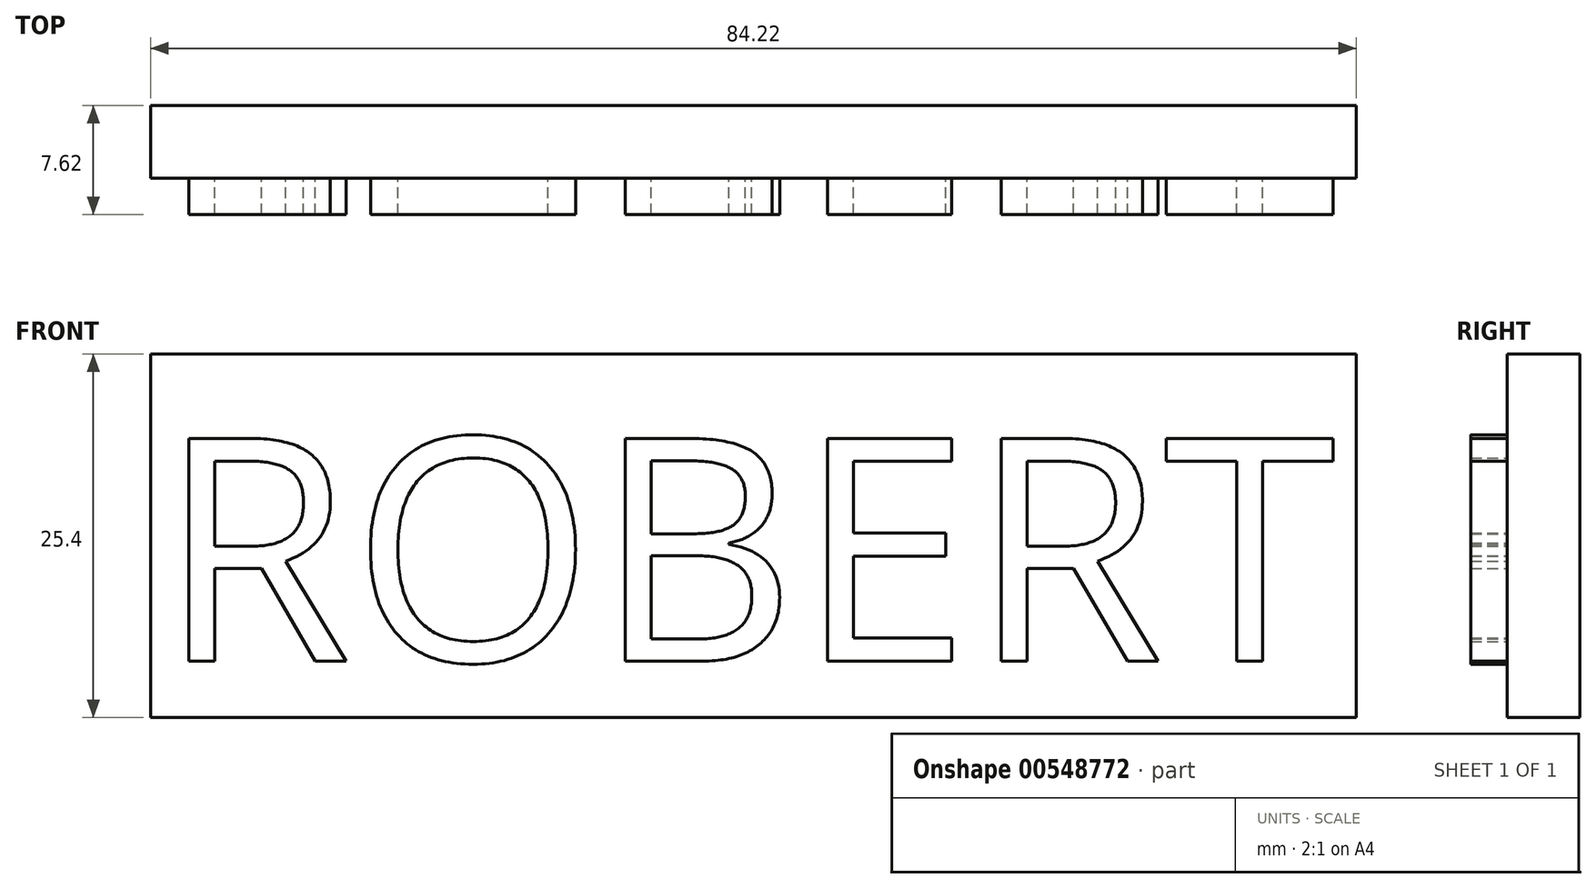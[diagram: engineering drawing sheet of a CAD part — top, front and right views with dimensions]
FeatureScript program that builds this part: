
annotation { "Feature Type Name" : "Feature", "Feature Type Description" : "" }
export const myFeature = defineFeature(function(context is Context, id is Id, definition is map)
    precondition{}
    {
        {
            var Q0;
            Q0=qCreatedBy(makeId("Front.planeOp"),FACE);
            var sketch = newSketch(context, id + "F0", { "sketchPlane" : qUnion([Q0])});
            skLineSegment(sketch, "E0.bottom", {"start": v(-42.11, -12.7) * mm, "end": v(42.11, -12.7) * mm});
            skLineSegment(sketch, "E0.top", {"start": v(-42.11, 12.7) * mm, "end": v(42.11, 12.7) * mm});
            skLineSegment(sketch, "E0.left", {"start": v(-42.11, -12.7) * mm, "end": v(-42.11, 12.7) * mm});
            skLineSegment(sketch, "E0.right", {"start": v(42.11, -12.7) * mm, "end": v(42.11, 12.7) * mm});
            skPoint(sketch, "E0.middle", {"position": v(0, 0) * mm});
            skSolve(sketch);
        }
        {
            var Q0;
            Q0=makeQuery(id+"F0.imprint","IMPRINT",FACE,{"disambiguationData":[TD([[makeQuery(id+"F0.imprint","IMPRINT",EDGE,{"derivedFrom":sQuery(id+"F0.wireOp",EDGE,"E0.bottom")}),1.0]])]});
            extrude(context, id + "F1", {"entities" : qUnion([Q0]), "depth" : 5.08 * mm, "offsetDistance" : 25.4 * mm});
        }
        {
            var Q0;
            Q0=makeQuery(id+"F1.opExtrude","CAP_FACE",FACE,{"disambiguationData":[OSD([sQuery(id+"F0.wireOp",EDGE,"E0.bottom"),sQuery(id+"F0.wireOp",EDGE,"E0.top"),sQuery(id+"F0.wireOp",EDGE,"E0.left"),sQuery(id+"F0.wireOp",EDGE,"E0.right")])],"isStart":false});
            var sketch = newSketch(context, id + "F2", { "sketchPlane" : qUnion([Q0])});
            skText(sketch, "E1", { "text": "ROBERT", "fontName": "OpenSans-Regular.ttf"});
            const initialGuessF2  = {"E1": [-0.04156, -0.00876, 1, 0, 0.0157]};
            skSetInitialGuess(sketch, initialGuessF2);
            skSolve(sketch);
        }
        {
            var Q0;
            Q0 = qSketchRegion(id + "F2", true);
            extrude(context, id + "F3", {"entities" : qUnion([Q0]), "operationType" : NewBodyOperationType.ADD, "depth" : 2.54 * mm, "offsetDistance" : 25.4 * mm});
        }
    });
